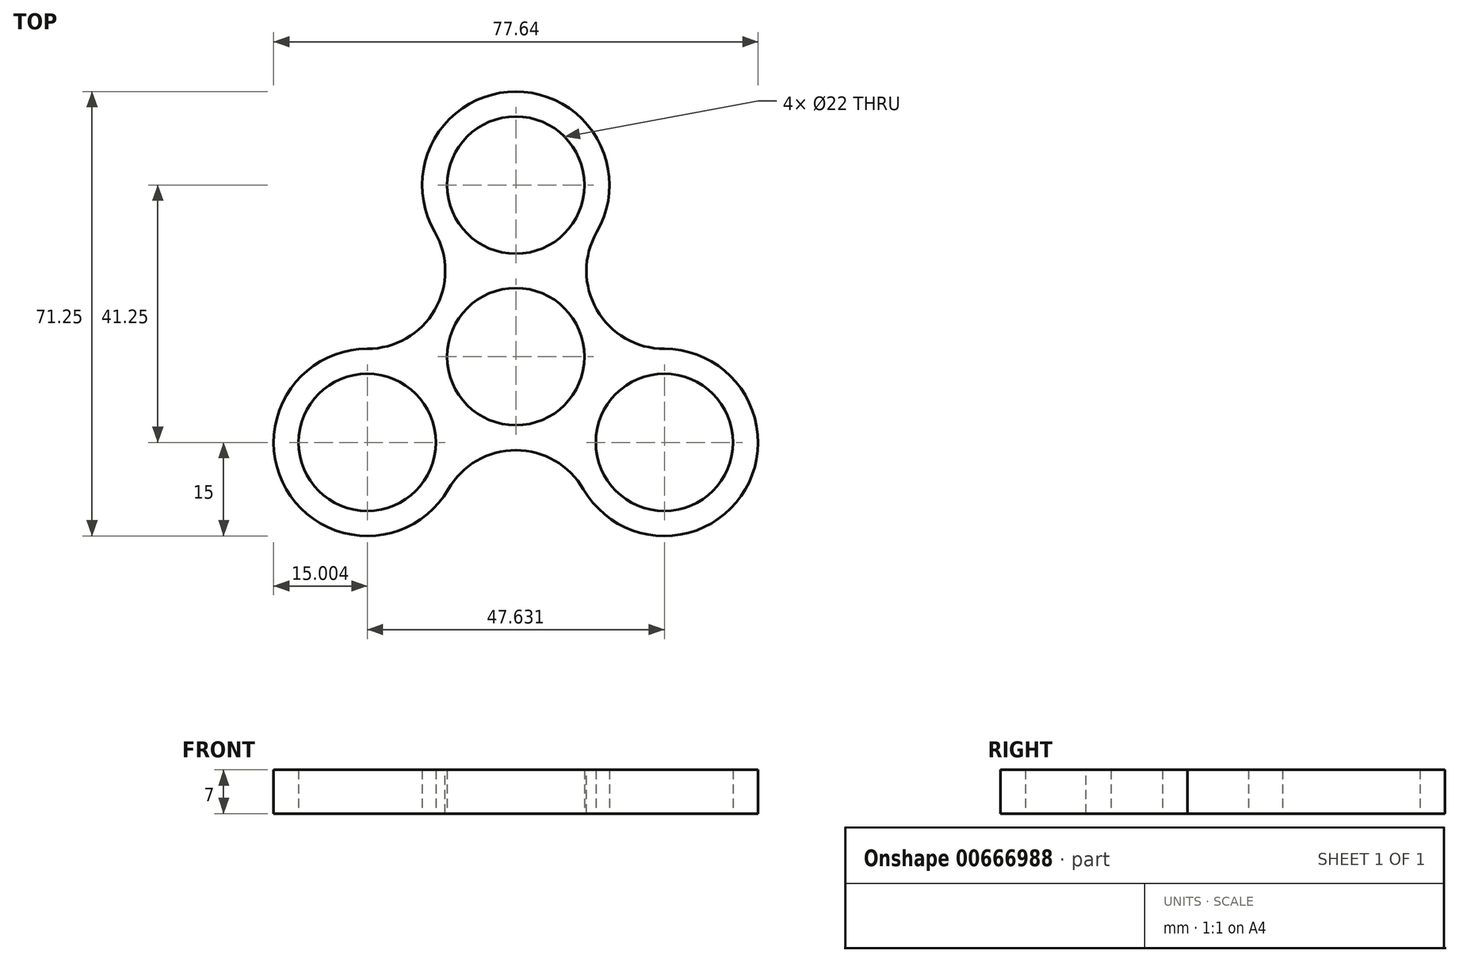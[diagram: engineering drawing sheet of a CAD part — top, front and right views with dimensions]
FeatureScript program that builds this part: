
annotation { "Feature Type Name" : "Feature", "Feature Type Description" : "" }
export const myFeature = defineFeature(function(context is Context, id is Id, definition is map)
    precondition{}
    {
        {
            var Q0;
            Q0=qCreatedBy(makeId("Top.planeOp"),FACE);
            var sketch = newSketch(context, id + "F0", { "sketchPlane" : qUnion([Q0])});
            skCircle(sketch, "E0", {"center": v(0, 0) * mm, "radius": 11 * mm});
            skLineSegment(sketch, "E1", {"start": v(0, 0) * mm, "end": v(0, 27.5) * mm, "construction": true});
            skCircle(sketch, "E2", {"center": v(0, 27.5) * mm, "radius": 11 * mm});
            skCircle(sketch, "E3.1.0", {"center": v(-23.82, -13.75) * mm, "radius": 11 * mm});
            skCircle(sketch, "E3.2.0", {"center": v(23.82, -13.75) * mm, "radius": 11 * mm});
            skCircle(sketch, "E4", {"center": v(0, 0) * mm, "radius": 15 * mm});
            skCircle(sketch, "E5", {"center": v(0, 27.5) * mm, "radius": 15 * mm});
            skCircle(sketch, "E6.1.0", {"center": v(-23.82, -13.75) * mm, "radius": 15 * mm});
            skCircle(sketch, "E6.2.0", {"center": v(23.82, -13.75) * mm, "radius": 15 * mm});
            skSolve(sketch);
        }
        {
            var Q0;
            Q0=qSketchRegion(id+"F0",true);
            extrude(context, id + "F1", {"entities" : qUnion([Q0]), "depth" : 7 * mm, "offsetDistance" : 25 * mm});
        }
        {
            var Q0;
            {var subQ0=sQuery(id+"F0.wireOp",EDGE,"E5");var subQ1=sQuery(id+"F0.wireOp",EDGE,"E4");Q0=makeQuery(id+"F1.opExtrude","SWEPT_EDGE",EDGE,{"disambiguationData":[OSD([subQ1,subQ0]),TDD([makeQuery(id+"F0.imprint","INTERSECT",VERTEX,{"disambiguationData":[OD(1.0)],"derivedFrom":[subQ1,subQ0]})])]});}
            var Q1;
            {var subQ0=sQuery(id+"F0.wireOp",EDGE,"E6.2.0");var subQ1=sQuery(id+"F0.wireOp",EDGE,"E4");Q1=makeQuery(id+"F1.opExtrude","SWEPT_EDGE",EDGE,{"disambiguationData":[OSD([subQ1,subQ0]),TDD([makeQuery(id+"F0.imprint","INTERSECT",VERTEX,{"disambiguationData":[OD(1.0)],"derivedFrom":[subQ1,subQ0]})])]});}
            var Q2;
            {var subQ0=sQuery(id+"F0.wireOp",EDGE,"E6.1.0");var subQ1=sQuery(id+"F0.wireOp",EDGE,"E4");Q2=makeQuery(id+"F1.opExtrude","SWEPT_EDGE",EDGE,{"disambiguationData":[OSD([subQ1,subQ0]),TDD([makeQuery(id+"F0.imprint","INTERSECT",VERTEX,{"disambiguationData":[OD(0.0)],"derivedFrom":[subQ1,subQ0]})])]});}
            var Q3;
            {var subQ0=sQuery(id+"F0.wireOp",EDGE,"E5");var subQ1=sQuery(id+"F0.wireOp",EDGE,"E4");Q3=makeQuery(id+"F1.opExtrude","SWEPT_EDGE",EDGE,{"disambiguationData":[OSD([subQ1,subQ0]),TDD([makeQuery(id+"F0.imprint","INTERSECT",VERTEX,{"disambiguationData":[OD(0.0)],"derivedFrom":[subQ1,subQ0]})])]});}
            var Q4;
            {var subQ0=sQuery(id+"F0.wireOp",EDGE,"E6.1.0");var subQ1=sQuery(id+"F0.wireOp",EDGE,"E4");Q4=makeQuery(id+"F1.opExtrude","SWEPT_EDGE",EDGE,{"disambiguationData":[OSD([subQ1,subQ0]),TDD([makeQuery(id+"F0.imprint","INTERSECT",VERTEX,{"disambiguationData":[OD(1.0)],"derivedFrom":[subQ1,subQ0]})])]});}
            var Q5;
            {var subQ0=sQuery(id+"F0.wireOp",EDGE,"E6.2.0");var subQ1=sQuery(id+"F0.wireOp",EDGE,"E4");Q5=makeQuery(id+"F1.opExtrude","SWEPT_EDGE",EDGE,{"disambiguationData":[OSD([subQ1,subQ0]),TDD([makeQuery(id+"F0.imprint","INTERSECT",VERTEX,{"disambiguationData":[OD(0.0)],"derivedFrom":[subQ1,subQ0]})])]});}
            fillet(context, id + "F2", {"entities" : qUnion([Q0, Q1, Q2, Q3, Q4, Q5]), "radius" : 12.5 * mm, "tangentPropagation" : true, "allowEdgeOverflow" : false});
        }
    });
